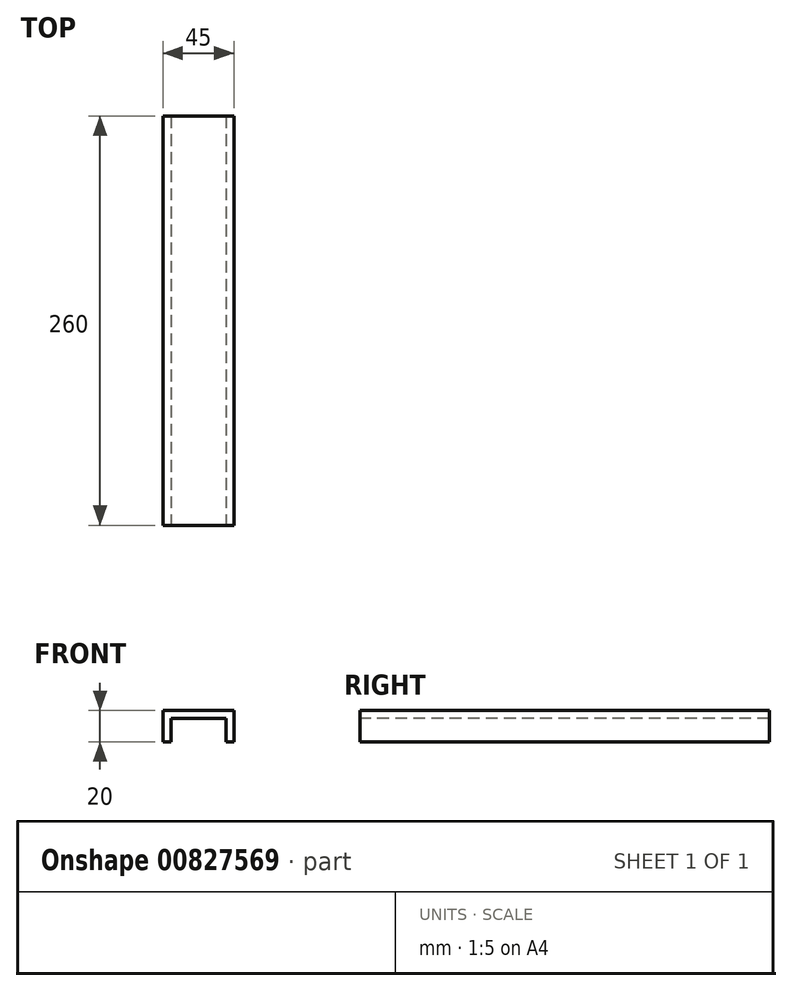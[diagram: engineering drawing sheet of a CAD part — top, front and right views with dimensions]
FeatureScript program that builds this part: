
annotation { "Feature Type Name" : "Feature", "Feature Type Description" : "" }
export const myFeature = defineFeature(function(context is Context, id is Id, definition is map)
    precondition{}
    {
        {
            var Q0;
            Q0=qCreatedBy(makeId("Front.planeOp"),FACE);
            var sketch = newSketch(context, id + "F0", { "sketchPlane" : qUnion([Q0])});
            skLineSegment(sketch, "E0.bottom", {"start": v(-22.5, 10) * mm, "end": v(22.5, 10) * mm});
            skLineSegment(sketch, "E0.top", {"start": v(-22.5, -10) * mm, "end": v(-17.5, -10) * mm});
            skLineSegment(sketch, "E0.left", {"start": v(-22.5, 10) * mm, "end": v(-22.5, -10) * mm});
            skLineSegment(sketch, "E0.right", {"start": v(22.5, 10) * mm, "end": v(22.5, -10) * mm});
            skPoint(sketch, "E0.middle", {"position": v(0, 0) * mm});
            skLineSegment(sketch, "E1.0", {"start": v(-17.5, 5) * mm, "end": v(17.5, 5) * mm});
            skLineSegment(sketch, "E2.0", {"start": v(-17.5, 5) * mm, "end": v(-17.5, -10) * mm});
            skLineSegment(sketch, "E3.0", {"start": v(17.5, 5) * mm, "end": v(17.5, -10) * mm});
            skLineSegment(sketch, "E4.trimOffspring", {"start": v(17.5, -10) * mm, "end": v(22.5, -10) * mm});
            skSolve(sketch);
        }
        {
            var Q0;
            Q0=makeQuery(id+"F0.imprint","IMPRINT",FACE,{"disambiguationData":[TD([[makeQuery(id+"F0.imprint","IMPRINT",EDGE,{"derivedFrom":sQuery(id+"F0.wireOp",EDGE,"E0.bottom")}),-1.0]])]});
            extrude(context, id + "F1", {"entities" : qUnion([Q0]), "oppositeDirection" : true, "depth" : 260 * mm, "offsetDistance" : 25 * mm});
        }
    });
